# Revit family: Doors_Fire-Doors-Shutters_Wayne-Dalton_Fire-Rated-Counter-Shutters-FireStar-Model-540_
name_source: partatom
category: Specialty Equipment
units: mm (PartAtom-declared; Revit-internal decimal feet)

## family parameters
Always vertical = Yes
Cut with Voids When Loaded = Yes
Host = Wall
OmniClass Number = 23.30.10.21.34
OmniClass Title = Industrial Doors
Part Type = Normal
Room Calculation Point = No
Round Connector Dimension = Use Diameter
Shared = No

## types (9) — shared parameters
Description = Firestar Model 540 Fire Rated Counter Shutter
Finish Material = Finish - Wayne Dalton - Black
Lookup Table = Hood Dimensions
Manufacturer = Wayne Dalton
Model = 540
Powder Coat (Note) = Wayne Dalton also offers approximately 200 RAL powder coat options to complement the exterior colors of a building.
Power Factor = 1
Product Guid = 1921f86f-db44-4d7a-8f35-b5c0a0cfdcec
Product Page URL = https://www.wayne-dalton.com
Product data url = https://www.bimobject.com
URL = https://www.wayne-dalton.com
Wall Closure = By host

## per-type parameters (varying)
| type | Apparent Load Phase 1 | Apparent Load Phase 2 | Apparent Load Phase 3 | Crank | Current | Electric Operator | Frequency | Manual | Number of Poles | Operator Visibility | Voltage |
| 115 volts, one phase, 60 Hz (110-120V range) | 2300 VA | 0 VA | 0 VA | No | 20 A | Yes | 60 Hz | No | 1 | Yes | 115 V |
| ‏​Manual push-up | 0 VA | 0 VA | 0 VA | No | 0 A | No | 0 Hz | Yes | 1 | No | 0 V |
| 230 volts, three phase, 60 Hz (208-245V range) | 2656 VA | 2656 VA | 2656 VA | No | 20 A | Yes | 60 Hz | No | 3 | Yes | 230 V |
| 230 volts, one phase, 60 Hz (208-245V range) | 4600 VA | 0 VA | 0 VA | No | 20 A | Yes | 60 Hz | No | 1 | Yes | 230 V |
| 460 volts, three phase, 60 Hz (456-495V range) | 5312 VA | 5312 VA | 5312 VA | No | 20 A | Yes | 60 Hz | No | 3 | Yes | 460 V |
| 208 volts, one phase, 60 Hz (190-207V range) | 4160 VA | 0 VA | 0 VA | No | 20 A | Yes | 60 Hz | No | 1 | Yes | 208 V |
| 208 volts, three phase, 60 Hz (190-207V range) | 2402 VA | 2402 VA | 2402 VA | No | 20 A | Yes | 60 Hz | No | 3 | Yes | 208 V |
| 575 volts, three phase, 60 Hz | 6640 VA | 6640 VA | 6640 VA | No | 20 A | Yes | 60 Hz | No | 3 | Yes | 575 V |
| Manual crank | 0 VA | 0 VA | 0 VA | Yes | 0 A | No | 0 Hz | No | 1 | Yes | 0 V |

## geometry (parser evidence)
native form markers: Sweep x14
no freeform markers — native parametric forms only
